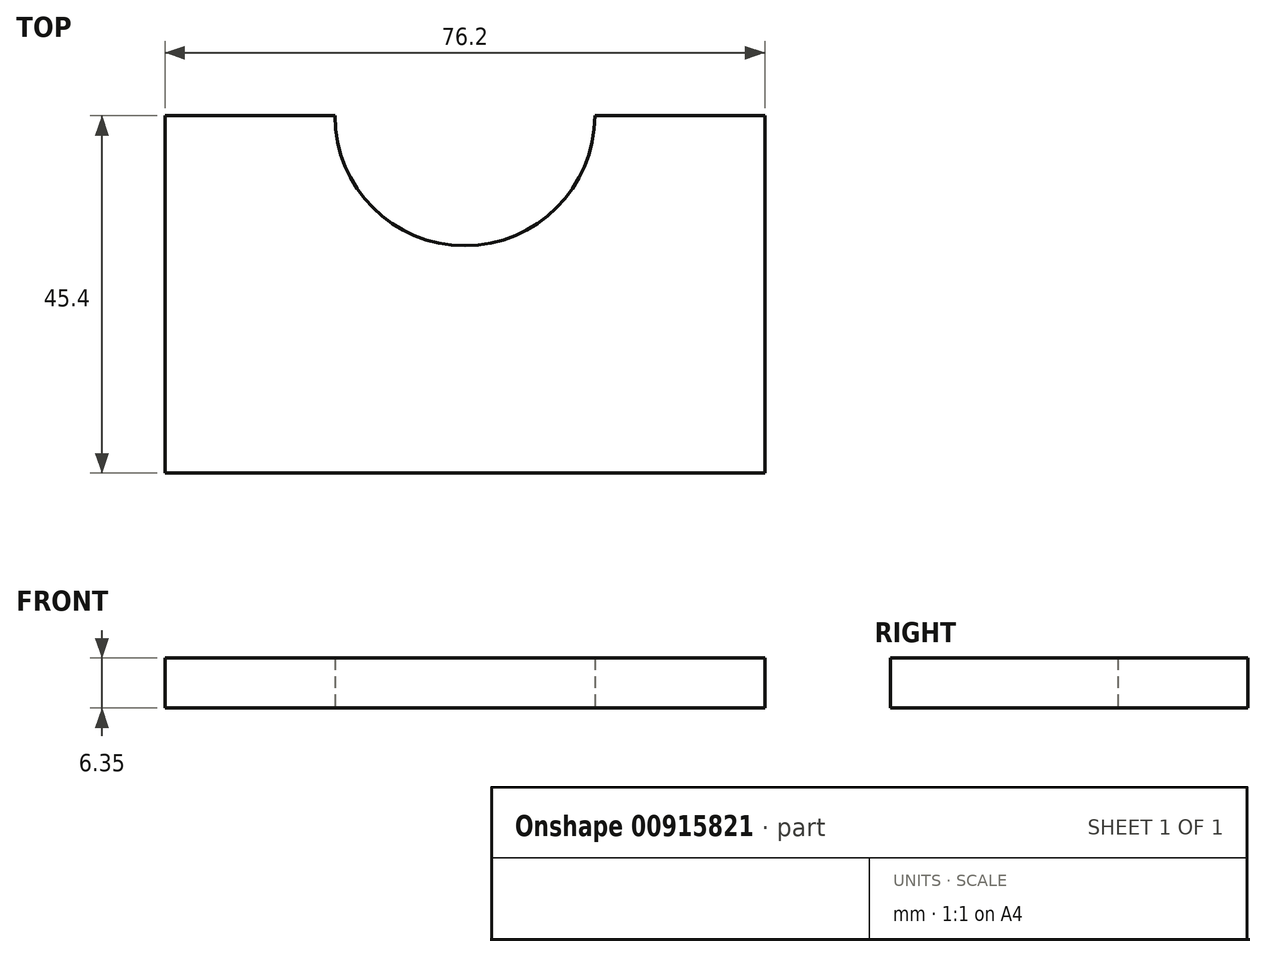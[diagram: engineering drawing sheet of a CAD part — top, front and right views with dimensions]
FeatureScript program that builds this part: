
annotation { "Feature Type Name" : "Feature", "Feature Type Description" : "" }
export const myFeature = defineFeature(function(context is Context, id is Id, definition is map)
    precondition{}
    {
        {
            var Q0;
            Q0=qCreatedBy(makeId("Top.planeOp"),FACE);
            var sketch = newSketch(context, id + "F0", { "sketchPlane" : qUnion([Q0])});
            skLineSegment(sketch, "E0.bottom", {"start": v(0, 0) * mm, "end": v(21.59, 0) * mm});
            skLineSegment(sketch, "E0.top", {"start": v(0, -45.4) * mm, "end": v(76.2, -45.4) * mm});
            skLineSegment(sketch, "E0.left", {"start": v(0, 0) * mm, "end": v(0, -45.4) * mm});
            skLineSegment(sketch, "E0.right", {"start": v(76.2, 0) * mm, "end": v(76.2, -45.4) * mm});
            skArc(sketch, "E1", {"start": v(21.59, 0) * mm, "mid": v(38.1, -16.51) * mm, "end": v(54.61, 0) * mm});
            skLineSegment(sketch, "E2.trimOffspring", {"start": v(54.61, 0) * mm, "end": v(76.2, 0) * mm});
            skSolve(sketch);
        }
        {
            var Q0;
            Q0=makeQuery(id+"F0.imprint","IMPRINT",FACE,{"disambiguationData":[TD([[makeQuery(id+"F0.imprint","IMPRINT",EDGE,{"derivedFrom":sQuery(id+"F0.wireOp",EDGE,"E0.bottom")}),-1.0]])]});
            extrude(context, id + "F1", {"entities" : qUnion([Q0]), "depth" : 6.35 * mm, "offsetDistance" : 25.4 * mm});
        }
    });
